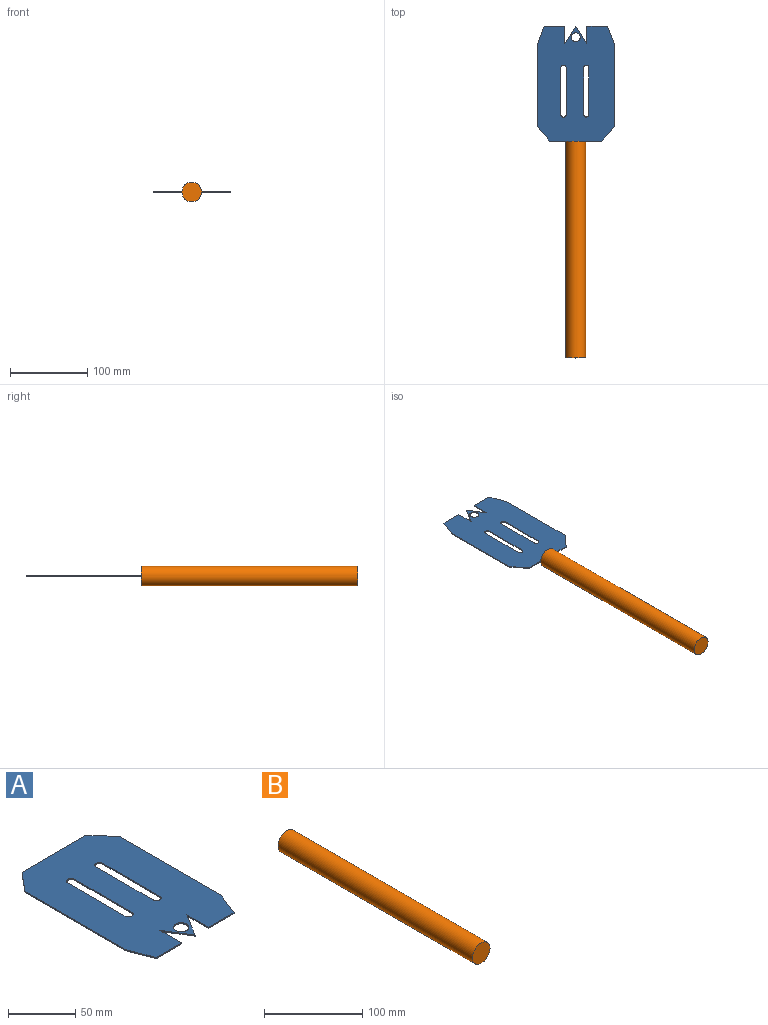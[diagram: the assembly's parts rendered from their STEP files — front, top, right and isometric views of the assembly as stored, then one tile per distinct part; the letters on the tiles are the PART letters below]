
ASSEMBLY  parts=2 mates=1
PART A: 24 faces, bbox 100x148.5x1 mm
  f0: plane 148.52x100mm, normal (0,0,1), area 12987.7mm2, adj f2,f3,f4,f5,f6,f7,f8,f9
  f1: plane 148.52x100mm, normal (0,0,-1), area 12987.7mm2, adj f2,f3,f4,f5,f6,f7,f8,f9
  f2: plane 23x1mm, normal (-1,0,0), area 23mm2, adj f0,f1,f3,f14
  f3: plane 26.82x1mm, normal (0,-1,0), area 26.8mm2, adj f0,f1,f2,f4
  f4: plane 23.24x9.22mm, normal (0.93,-0.37,0), area 25mm2, adj f0,f1,f3,f5
  f5: plane 106.67x1mm, normal (1,0,0), area 106.7mm2, adj f0,f1,f4,f6
  f6: plane 18.62x16.68mm, normal (0.74,0.67,0), area 25mm2, adj f0,f1,f5,f7
  f7: plane 67.29x1mm, normal (0,1,0), area 67.3mm2, adj f0,f1,f6,f8
  f8: plane 19.19x16.02mm, normal (-0.77,0.64,0), area 25mm2, adj f0,f1,f7,f9
  f9: plane 105.95x1mm, normal (-1,0,0), area 105.9mm2, adj f0,f1,f8,f10
  f10: plane 23.38x8.84mm, normal (-0.94,-0.35,0), area 25mm2, adj f0,f1,f9,f11
  f11: plane 26.82x1mm, normal (0,-1,0), area 26.8mm2, adj f0,f1,f10,f12
  f12: plane 23x1mm, normal (1,0,0), area 23mm2, adj f0,f1,f11,f13
  f13: plane 23x14.14mm, normal (-0.85,-0.52,0), area 27mm2, adj f0,f1,f12,f14
  f14: plane 23x14.14mm, normal (0.85,-0.52,0), area 27mm2, adj f0,f1,f2,f13
  f15: plane 60x1mm, normal (1,0,0), area 60mm2, adj f0,f1,f16,f18
  f16: cylinder r=3.52mm len=7.03mm, axis (0,0,1), area 11mm2, adj f0,f1,f15,f17
  f17: plane 60x1mm, normal (-1,0,0), area 60mm2, adj f0,f1,f16,f18
  f18: cylinder r=3.52mm len=7.03mm, axis (0,0,1), area 11mm2, adj f0,f1,f15,f17
  f19: plane 60x1mm, normal (-1,0,0), area 60mm2, adj f0,f1,f20,f22
  f20: cylinder r=3.47mm len=6.93mm, axis (0,0,1), area 10.9mm2, adj f0,f1,f19,f21
  f21: plane 60x1mm, normal (1,0,0), area 60mm2, adj f0,f1,f20,f22
  f22: cylinder r=3.47mm len=6.93mm, axis (0,0,1), area 10.9mm2, adj f0,f1,f19,f21
  f23: cylinder r=5.79mm len=11.58mm, axis (0,0,1), area 36.4mm2, adj f0,f1
PART B: 3 faces, bbox 25.4x280x25.4 mm
  f0: cylinder r=12.7mm len=280mm, axis (0,1,0), area 22343mm2, adj f1,f2
  f1: plane 25.4x25.4mm, normal (0,-1,0), area 506.7mm2, adj f0
  f2: plane 25.4x25.4mm, normal (0,1,0), area 506.7mm2, adj f0
PLACE A rot(axis=(1,0,0),180deg) t=(-119.39,181.56,105.32)mm
PLACE B t=(-44.77,111.14,71.51)mm
MATE fastened A.f7 <-> B.f0  axis (0,-1,0) through (-112.97,111.14,104.82)mm
